# Revit family: PRD_FrankeWS_MxrTps_HygieneUnit_ACLM9001
name_source: partatom
category: Specialty Equipment
revit_build: Autodesk Revit 2018 (Build: 20190510_1515(x64)
units: mm (PartAtom-declared; Revit-internal decimal feet)

## family parameters
Always vertical = No
Cut with Voids When Loaded = No
OmniClass Number = 23.45.05.14.99
OmniClass Title = Other Sanitary Washing Plumbing Fixtures
Part Type = Normal
Room Calculation Point = No
Round Connector Dimension = Use Diameter
Shared = No
Work Plane-Based = Yes

## types (1)
- ACLM9001
    AssetType = Fixed
    BIMObjectName = PRD_AR_MixerTaps_HygieneUnit_ACLM9001
    BodyMaterial = PRD_AR_ChromatedBrass_HighPolished
    Category = Pr_40_20_87_55, Mixer taps
    Default Elevation = 1219 mm
    Description = Hygiene unit for F5L-Mix single-lever mixers as wall mixers for sanitary and shower facilities, for performing of automatic hygiene flushing and program-controlled thermal disinfection (additional bypass solenoid cartridge necessary) and storage of statistical data. Housing adapter including sensor with control electronics and 6 V lithium battery (CR-P2) as well as function block with solenoid valve cartridge. Activated water hygiene flushing (30 seconds), fixed interval time 24 hours and saving of statistical data. With option for parameterization and communication via optional, bidirectional remote control.
    DurationUnit = year
    Features = for performing of automatic hygiene flushing and program-controlled thermal disinfection (additional bypass solenoid cartridge necessary) and storage of statistical data
    GrossWeight = 0.90 kg
    IfcExportAs = IfcController
    IfcExportType = USERDEFINED
    Manufacturer = KWC Group AG
    ManufacturerName = KWC Group AG
    ManufacturerURL = www.kwc.com
    Model = ACLM9001
    ModelNumber = 2030039446
    ModelReference = ACLM9001
    Name = Hygiene unit ACLM9001
    NetWeight = 0.84 kg
    NominalDepth = 0 mm  [stored 0 ft]
    NominalHeight = 0 mm  [stored 0 ft]
    NominalWidth = 0 mm  [stored 0 ft]
    ProductInformation = https://pim.kwc.com
    Quantity = 1
    QuantityUom = Piece
    SensorMaterial = PRD_AR_Black
    Status = New
    URL = www.kwc.com
    Uniclass2015Code = Pr_40_20_87_55
    Uniclass2015Title = Mixer taps
    Uniclass2015Version = Products v1.17
    Version = 1
    WarrantyDurationUnit = year

note: [stored X ft] marks values corroborated as IEEE doubles in the binary element streams (Revit-internal decimal feet)

## geometry (parser evidence)
native form markers: Sweep x3
no freeform markers — native parametric forms only
